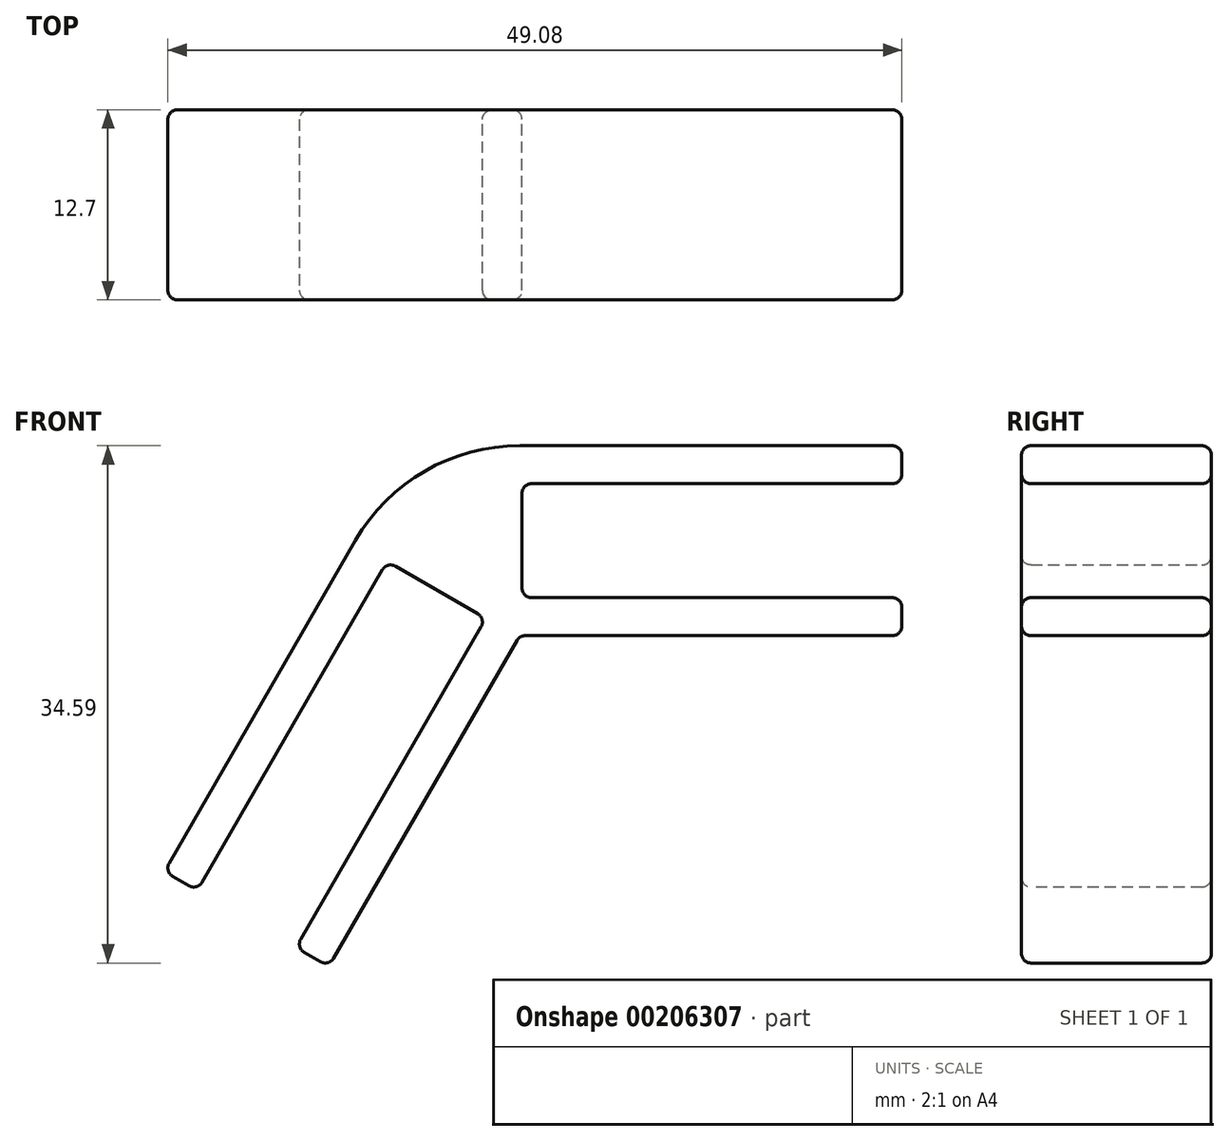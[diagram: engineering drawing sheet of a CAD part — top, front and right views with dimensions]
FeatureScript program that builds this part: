
annotation { "Feature Type Name" : "Feature", "Feature Type Description" : "" }
export const myFeature = defineFeature(function(context is Context, id is Id, definition is map)
    precondition{}
    {
        {
            var Q0;
            Q0=qCreatedBy(makeId("Front.planeOp"),FACE);
            var sketch = newSketch(context, id + "F0", { "sketchPlane" : qUnion([Q0])});
            skLineSegment(sketch, "E0.1", {"start": v(29.21, 3.81) * mm, "end": v(4.45, 3.81) * mm});
            skLineSegment(sketch, "E0.4", {"start": v(4.44, -3.81) * mm, "end": v(29.21, -3.8) * mm});
            skLineSegment(sketch, "E1", {"start": v(3.67, 6.35) * mm, "end": v(29.2, 6.35) * mm});
            skLineSegment(sketch, "E2", {"start": v(29.21, -6.35) * mm, "end": v(3.67, -6.35) * mm});
            skLineSegment(sketch, "E3", {"start": v(29.21, 3.81) * mm, "end": v(29.21, 6.35) * mm});
            skLineSegment(sketch, "E4", {"start": v(29.21, -6.35) * mm, "end": v(29.21, -3.8) * mm});
            skLineSegment(sketch, "E5", {"start": v(3.81, 3.18) * mm, "end": v(3.81, -3.18) * mm});
            skArc(sketch, "E6.filletArc", {"start": v(4.45, 3.81) * mm, "mid": v(4, 3.62) * mm, "end": v(3.81, 3.18) * mm});
            skArc(sketch, "E7.filletArc", {"start": v(3.8, -3.18) * mm, "mid": v(4, -3.62) * mm, "end": v(4.44, -3.81) * mm});
            skPoint(sketch, "E8", {"position": v(3.81, 0) * mm});
            skLineSegment(sketch, "E9.1.0", {"start": v(-5.52, -1.94) * mm, "end": v(-17.9, -23.4) * mm});
            skLineSegment(sketch, "E9.1.1", {"start": v(-11.3, -27.2) * mm, "end": v(1.08, -5.75) * mm});
            skLineSegment(sketch, "E9.1.2", {"start": v(-11.3, -27.2) * mm, "end": v(-9.1, -28.47) * mm});
            skLineSegment(sketch, "E9.1.3", {"start": v(0.84, -4.89) * mm, "end": v(-4.65, -1.71) * mm});
            skLineSegment(sketch, "E9.1.4", {"start": v(-20.1, -22.12) * mm, "end": v(-7.33, 0) * mm});
            skArc(sketch, "E9.1.5", {"start": v(1.08, -5.75) * mm, "mid": v(1.14, -5.27) * mm, "end": v(0.84, -4.89) * mm});
            skPoint(sketch, "E9.1.6", {"position": v(-1.9, -3.3) * mm});
            skLineSegment(sketch, "E9.1.7", {"start": v(-20.1, -22.12) * mm, "end": v(-17.9, -23.4) * mm});
            skLineSegment(sketch, "E9.1.8", {"start": v(3.67, -6.35) * mm, "end": v(-9.1, -28.47) * mm});
            skArc(sketch, "E9.1.9", {"start": v(-4.65, -1.71) * mm, "mid": v(-5.14, -1.65) * mm, "end": v(-5.52, -1.94) * mm});
            skPoint(sketch, "E9.center", {"position": v(0, 0) * mm});
            skLineSegment(sketch, "E9.anchor1", {"start": v(0, 0) * mm, "end": v(3.67, -6.35) * mm, "construction": true});
            skLineSegment(sketch, "E9.anchor2", {"start": v(0, 0) * mm, "end": v(-7.33, 0) * mm, "construction": true});
            skArc(sketch, "E10", {"start": v(3.67, 6.35) * mm, "mid": v(-2.68, 4.65) * mm, "end": v(-7.33, 0) * mm});
            skSolve(sketch);
        }
        {
            var Q0;
            Q0=makeQuery(id+"F0.imprint","IMPRINT",FACE,{"disambiguationData":[TD([[makeQuery(id+"F0.imprint","IMPRINT",EDGE,{"derivedFrom":sQuery(id+"F0.wireOp",EDGE,"E0.1")}),-1.0]])]});
            extrude(context, id + "F1", {"entities" : qUnion([Q0]), "depth" : 12.7 * mm});
        }
        {
            var Q0;
            Q0=makeQuery(id+"F1.opExtrude","CAP_FACE",FACE,{"disambiguationData":[OSD([sQuery(id+"F0.wireOp",EDGE,"E0.1"),sQuery(id+"F0.wireOp",EDGE,"E0.4"),sQuery(id+"F0.wireOp",EDGE,"E1"),sQuery(id+"F0.wireOp",EDGE,"E2"),sQuery(id+"F0.wireOp",EDGE,"E3"),sQuery(id+"F0.wireOp",EDGE,"E4"),sQuery(id+"F0.wireOp",EDGE,"E5"),sQuery(id+"F0.wireOp",EDGE,"E6.filletArc"),sQuery(id+"F0.wireOp",EDGE,"E7.filletArc"),sQuery(id+"F0.wireOp",EDGE,"E9.1.0"),sQuery(id+"F0.wireOp",EDGE,"E9.1.1"),sQuery(id+"F0.wireOp",EDGE,"E9.1.2"),sQuery(id+"F0.wireOp",EDGE,"E9.1.3"),sQuery(id+"F0.wireOp",EDGE,"E9.1.4"),sQuery(id+"F0.wireOp",EDGE,"E9.1.5"),sQuery(id+"F0.wireOp",EDGE,"E9.1.7"),sQuery(id+"F0.wireOp",EDGE,"E9.1.8"),sQuery(id+"F0.wireOp",EDGE,"E9.1.9"),sQuery(id+"F0.wireOp",EDGE,"E10")])],"isStart":false});
            var Q1;
            Q1=makeQuery(id+"F1.opExtrude","SWEPT_FACE",FACE,{"disambiguationData":[OSD([sQuery(id+"F0.wireOp",EDGE,"E3")])]});
            var Q2;
            Q2=makeQuery(id+"F1.opExtrude","SWEPT_FACE",FACE,{"disambiguationData":[OSD([sQuery(id+"F0.wireOp",EDGE,"E4")])]});
            var Q3;
            Q3=makeQuery(id+"F1.opExtrude","SWEPT_FACE",FACE,{"disambiguationData":[OSD([sQuery(id+"F0.wireOp",EDGE,"E9.1.8")])]});
            var Q4;
            Q4=makeQuery(id+"F1.opExtrude","CAP_FACE",FACE,{"disambiguationData":[OSD([sQuery(id+"F0.wireOp",EDGE,"E0.1"),sQuery(id+"F0.wireOp",EDGE,"E0.4"),sQuery(id+"F0.wireOp",EDGE,"E1"),sQuery(id+"F0.wireOp",EDGE,"E2"),sQuery(id+"F0.wireOp",EDGE,"E3"),sQuery(id+"F0.wireOp",EDGE,"E4"),sQuery(id+"F0.wireOp",EDGE,"E5"),sQuery(id+"F0.wireOp",EDGE,"E6.filletArc"),sQuery(id+"F0.wireOp",EDGE,"E7.filletArc"),sQuery(id+"F0.wireOp",EDGE,"E9.1.0"),sQuery(id+"F0.wireOp",EDGE,"E9.1.1"),sQuery(id+"F0.wireOp",EDGE,"E9.1.2"),sQuery(id+"F0.wireOp",EDGE,"E9.1.3"),sQuery(id+"F0.wireOp",EDGE,"E9.1.4"),sQuery(id+"F0.wireOp",EDGE,"E9.1.5"),sQuery(id+"F0.wireOp",EDGE,"E9.1.7"),sQuery(id+"F0.wireOp",EDGE,"E9.1.8"),sQuery(id+"F0.wireOp",EDGE,"E9.1.9"),sQuery(id+"F0.wireOp",EDGE,"E10")])],"isStart":true});
            var Q5;
            Q5=makeQuery(id+"F1.opExtrude","SWEPT_FACE",FACE,{"disambiguationData":[OSD([sQuery(id+"F0.wireOp",EDGE,"E9.1.2")])]});
            var Q6;
            Q6=makeQuery(id+"F1.opExtrude","SWEPT_FACE",FACE,{"disambiguationData":[OSD([sQuery(id+"F0.wireOp",EDGE,"E9.1.7")])]});
            fillet(context, id + "F2", {"entities" : qUnion([Q0, Q1, Q2, Q3, Q4, Q5, Q6]), "radius" : 0.64 * mm, "tangentPropagation" : true, "allowEdgeOverflow" : false});
        }
    });
